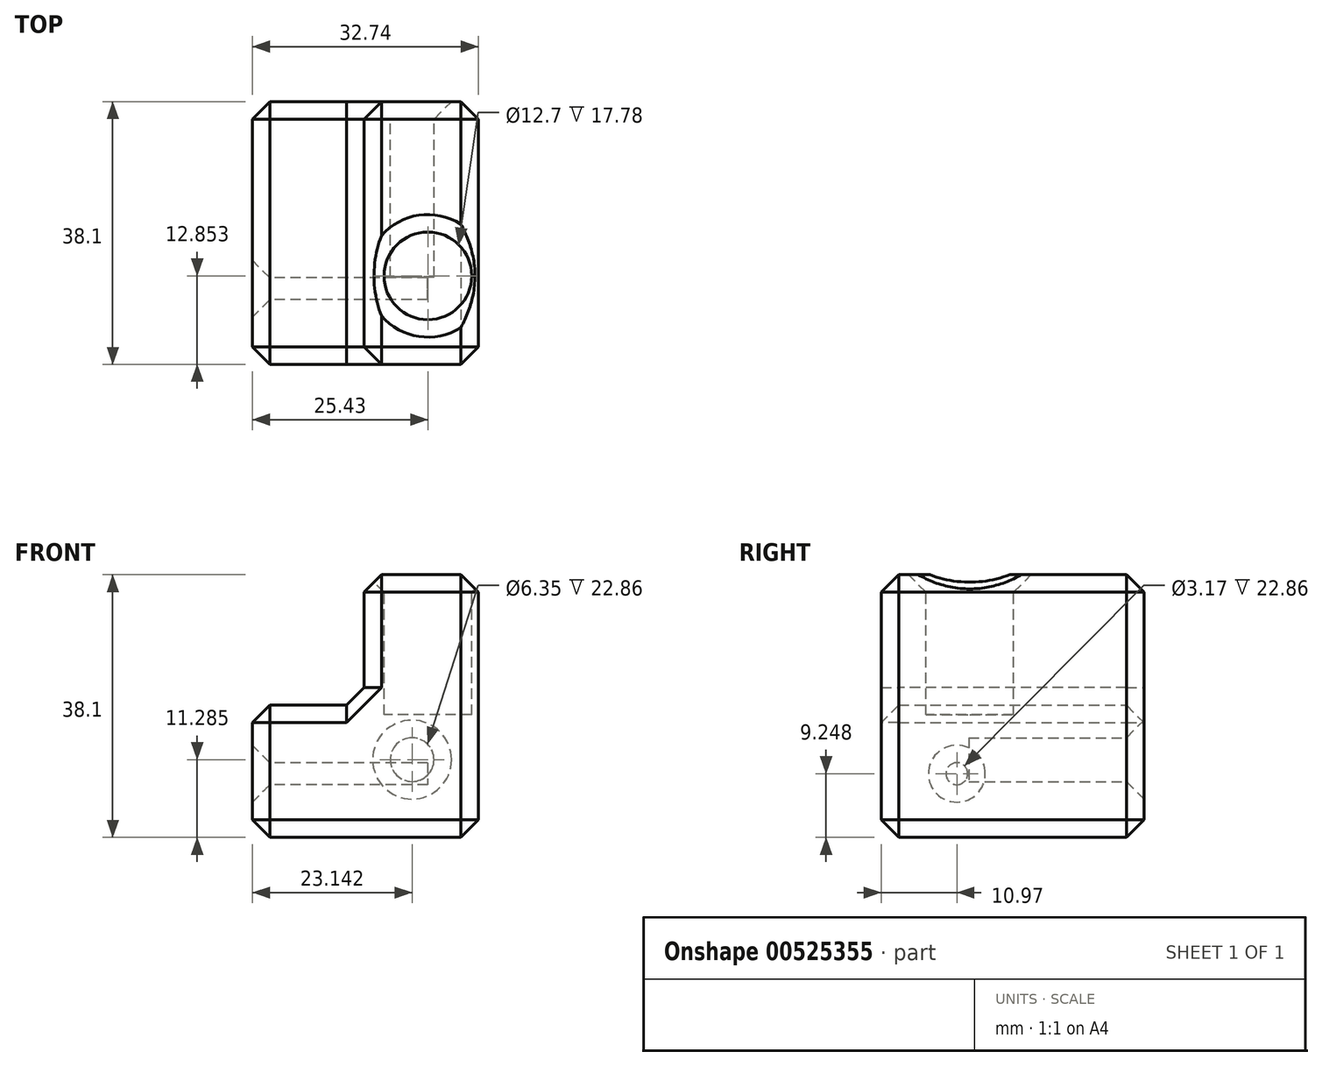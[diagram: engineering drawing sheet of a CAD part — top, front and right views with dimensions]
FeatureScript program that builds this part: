
annotation { "Feature Type Name" : "Feature", "Feature Type Description" : "" }
export const myFeature = defineFeature(function(context is Context, id is Id, definition is map)
    precondition{}
    {
        {
            var Q0;
            Q0=qCreatedBy(makeId("Front.planeOp"),FACE);
            var sketch = newSketch(context, id + "F0", { "sketchPlane" : qUnion([Q0])});
            skLineSegment(sketch, "E0.bottom", {"start": v(16.37, 19.05) * mm, "end": v(-16.37, 19.05) * mm});
            skLineSegment(sketch, "E0.top", {"start": v(16.37, -19.05) * mm, "end": v(-16.37, -19.05) * mm});
            skLineSegment(sketch, "E0.left", {"start": v(16.37, 19.05) * mm, "end": v(16.37, -19.05) * mm});
            skLineSegment(sketch, "E0.right", {"start": v(-16.37, 19.05) * mm, "end": v(-16.37, -19.05) * mm});
            skPoint(sketch, "E0.middle", {"position": v(0, 0) * mm});
            skSolve(sketch);
        }
        {
            var Q0;
            Q0=makeQuery(id+"F0.imprint","IMPRINT",FACE,{"disambiguationData":[TD([[makeQuery(id+"F0.imprint","IMPRINT",EDGE,{"derivedFrom":sQuery(id+"F0.wireOp",EDGE,"E0.bottom")}),1.0]])]});
            extrude(context, id + "F1", {"entities" : qUnion([Q0]), "depth" : 38.1 * mm, "offsetDistance" : 25.4 * mm});
        }
        {
            var Q0;
            Q0=makeQuery(id+"F1.opExtrude","CAP_FACE",FACE,{"disambiguationData":[OSD([sQuery(id+"F0.wireOp",EDGE,"E0.bottom"),sQuery(id+"F0.wireOp",EDGE,"E0.top"),sQuery(id+"F0.wireOp",EDGE,"E0.left"),sQuery(id+"F0.wireOp",EDGE,"E0.right")])],"isStart":true});
            var sketch = newSketch(context, id + "F2", { "sketchPlane" : qUnion([Q0])});
            skCircle(sketch, "E1", {"center": v(-6.77, -7.77) * mm, "radius": 3.18 * mm});
            skLineSegment(sketch, "E2.bottom", {"start": v(16.37, 19.45) * mm, "end": v(0.22, 19.45) * mm});
            skLineSegment(sketch, "E2.top", {"start": v(16.37, 0.14) * mm, "end": v(0.22, 0.14) * mm});
            skLineSegment(sketch, "E2.left", {"start": v(16.37, 19.45) * mm, "end": v(16.37, 0.14) * mm});
            skLineSegment(sketch, "E2.right", {"start": v(0.22, 19.45) * mm, "end": v(0.22, 0.14) * mm});
            skPoint(sketch, "E2.middle", {"position": v(8.3, 9.8) * mm});
            skSolve(sketch);
        }
        {
            var Q0;
            {var subQ0=sQuery(id+"F2.wireOp",EDGE,"E2.top");Q0=makeQuery(id+"F2.imprint","IMPRINT",FACE,{"disambiguationData":[TD([[makeQuery(id+"F2.imprint","IMPRINT",EDGE,{"derivedFrom":subQ0}),-1.0]])]});}
            extrude(context, id + "F3", {"entities" : qUnion([Q0]), "operationType" : NewBodyOperationType.REMOVE, "oppositeDirection" : true, "depth" : 38.1 * mm, "offsetDistance" : 25.4 * mm});
        }
        {
            var Q0;
            Q0 = qSketchRegion(id + "F2", true);
            extrude(context, id + "F4", {"entities" : qUnion([Q0]), "operationType" : NewBodyOperationType.REMOVE, "oppositeDirection" : true, "depth" : 25.4 * mm, "offsetDistance" : 25.4 * mm});
        }
        {
            var Q0;
            Q0=makeQuery(id+"F1.opExtrude","SWEPT_FACE",FACE,{"disambiguationData":[OSD([sQuery(id+"F0.wireOp",EDGE,"E0.bottom")])]});
            var sketch = newSketch(context, id + "F5", { "sketchPlane" : qUnion([Q0])});
            skCircle(sketch, "E3", {"center": v(9.06, -25.25) * mm, "radius": 6.35 * mm});
            skSolve(sketch);
        }
        {
            var Q0;
            Q0=makeQuery(id+"F5.imprint","IMPRINT",FACE,{"disambiguationData":[TD([[makeQuery(id+"F5.imprint","IMPRINT",EDGE,{"derivedFrom":sQuery(id+"F5.wireOp",EDGE,"E3")}),1.0]])]});
            extrude(context, id + "F6", {"entities" : qUnion([Q0]), "operationType" : NewBodyOperationType.REMOVE, "oppositeDirection" : true, "depth" : 20.32 * mm, "offsetDistance" : 25.4 * mm});
        }
        {
            var Q0;
            Q0=makeQuery(id+"F1.opExtrude","SWEPT_FACE",FACE,{"disambiguationData":[OSD([sQuery(id+"F0.wireOp",EDGE,"E0.right")])]});
            var sketch = newSketch(context, id + "F7", { "sketchPlane" : qUnion([Q0])});
            skCircle(sketch, "E4", {"center": v(27.13, -9.8) * mm, "radius": 1.59 * mm});
            skSolve(sketch);
        }
        {
            var Q0;
            Q0 = qSketchRegion(id + "F7", true);
            extrude(context, id + "F8", {"entities" : qUnion([Q0]), "operationType" : NewBodyOperationType.REMOVE, "oppositeDirection" : true, "depth" : 25.4 * mm, "offsetDistance" : 25.4 * mm});
        }
        {
            var Q0;
            Q0=makeQuery(id+"F1.opExtrude","SWEPT_FACE",FACE,{"disambiguationData":[OSD([sQuery(id+"F0.wireOp",EDGE,"E0.bottom")])]});
            var Q1;
            Q1=makeQuery(id+"F1.opExtrude","CAP_FACE",FACE,{"disambiguationData":[OSD([sQuery(id+"F0.wireOp",EDGE,"E0.bottom"),sQuery(id+"F0.wireOp",EDGE,"E0.top"),sQuery(id+"F0.wireOp",EDGE,"E0.left"),sQuery(id+"F0.wireOp",EDGE,"E0.right")])],"isStart":true});
            var Q2;
            Q2=makeQuery(id+"F3.boolean.opBoolean","COPY",FACE,{"derivedFrom":makeQuery(id+"F3.opExtrude","SWEPT_FACE",FACE,{"disambiguationData":[OSD([sQuery(id+"F2.wireOp",EDGE,"E2.right")])]})});
            var Q3;
            Q3=makeQuery(id+"F3.boolean.opBoolean","COPY",FACE,{"derivedFrom":makeQuery(id+"F3.opExtrude","SWEPT_FACE",FACE,{"disambiguationData":[OSD([sQuery(id+"F2.wireOp",EDGE,"E2.top")])]})});
            var Q4;
            Q4=makeQuery(id+"F1.opExtrude","SWEPT_FACE",FACE,{"disambiguationData":[OSD([sQuery(id+"F0.wireOp",EDGE,"E0.right")])]});
            var Q5;
            Q5=makeQuery(id+"F1.opExtrude","CAP_FACE",FACE,{"disambiguationData":[OSD([sQuery(id+"F0.wireOp",EDGE,"E0.bottom"),sQuery(id+"F0.wireOp",EDGE,"E0.top"),sQuery(id+"F0.wireOp",EDGE,"E0.left"),sQuery(id+"F0.wireOp",EDGE,"E0.right")])],"isStart":false});
            var Q6;
            Q6=makeQuery(id+"F1.opExtrude","SWEPT_FACE",FACE,{"disambiguationData":[OSD([sQuery(id+"F0.wireOp",EDGE,"E0.left")])]});
            chamfer(context, id + "F9", {"entities" : qUnion([Q0, Q1, Q2, Q3, Q4, Q5, Q6]), "width" : 2.54 * mm, "tangentPropagation" : true});
        }
    });
